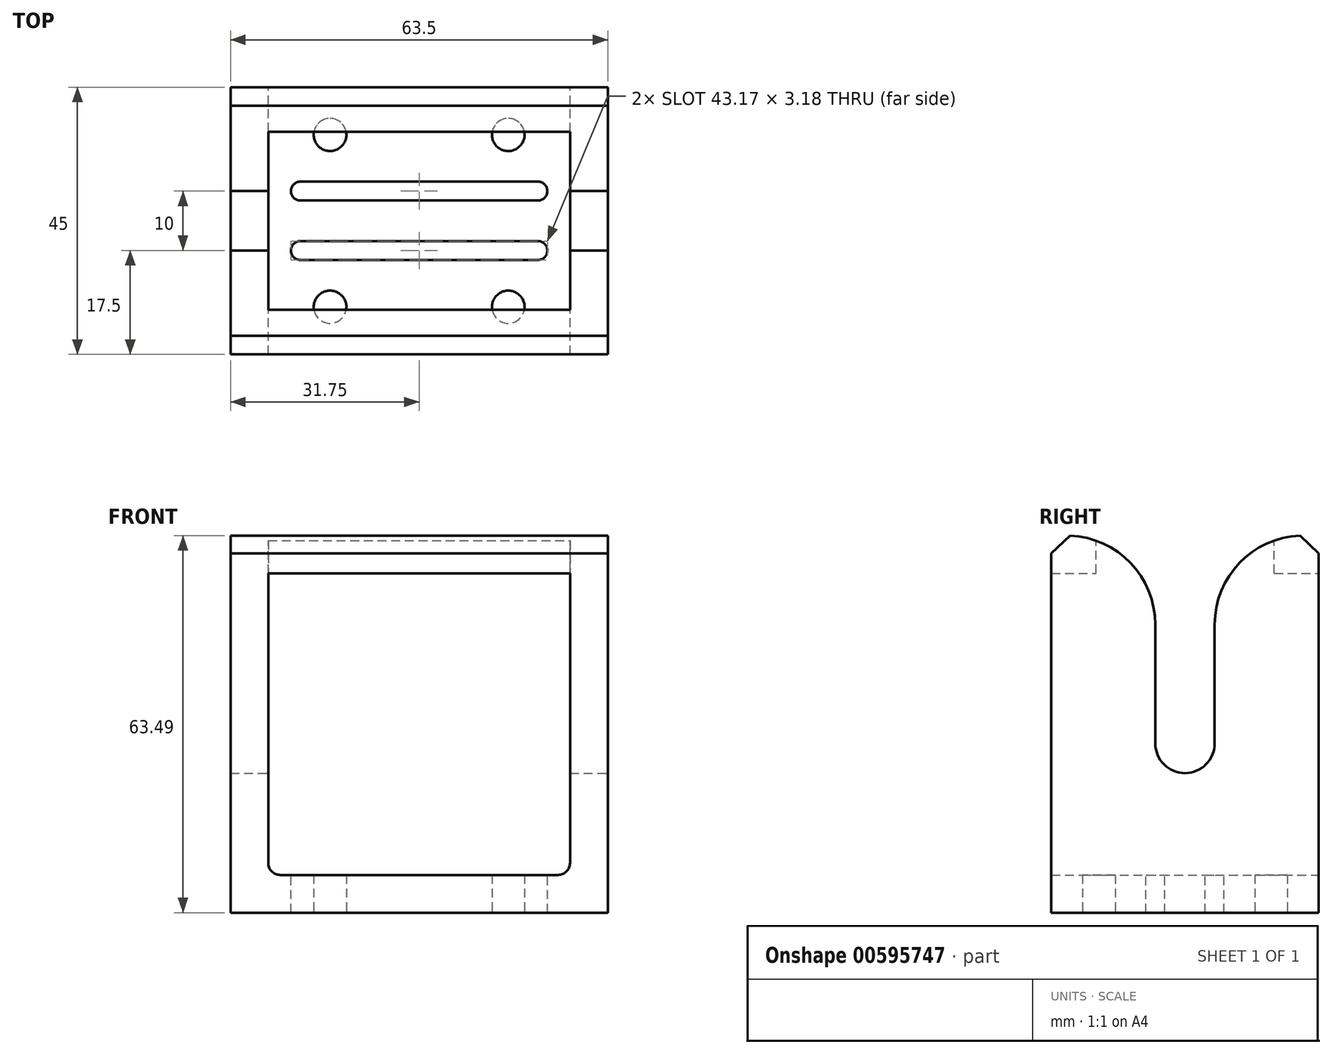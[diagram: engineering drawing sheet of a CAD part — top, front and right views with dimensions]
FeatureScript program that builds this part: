
annotation { "Feature Type Name" : "Feature", "Feature Type Description" : "" }
export const myFeature = defineFeature(function(context is Context, id is Id, definition is map)
    precondition{}
    {
        {
            var Q0;
            Q0=qCreatedBy(makeId("Front.planeOp"),FACE);
            var sketch = newSketch(context, id + "F0", { "sketchPlane" : qUnion([Q0])});
            skLineSegment(sketch, "E0", {"start": v(0, 0) * mm, "end": v(31.75, 0) * mm});
            skLineSegment(sketch, "E1", {"start": v(31.75, 0) * mm, "end": v(31.75, 63.5) * mm});
            skLineSegment(sketch, "E2", {"start": v(25.4, 57.15) * mm, "end": v(25.4, 6.35) * mm});
            skLineSegment(sketch, "E3", {"start": v(25.4, 6.35) * mm, "end": v(0, 6.35) * mm});
            skLineSegment(sketch, "E4", {"start": v(0, 6.35) * mm, "end": v(0, 0) * mm});
            skLineSegment(sketch, "E5", {"start": v(25.4, 57.15) * mm, "end": v(0, 57.15) * mm});
            skLineSegment(sketch, "E6", {"start": v(0, 57.15) * mm, "end": v(0, 63.5) * mm});
            skLineSegment(sketch, "E7", {"start": v(0, 63.5) * mm, "end": v(31.75, 63.5) * mm});
            skSolve(sketch);
        }
        {
            var Q0;
            Q0=makeQuery(id+"F0.imprint","IMPRINT",FACE,{"disambiguationData":[TD([[makeQuery(id+"F0.imprint","IMPRINT",EDGE,{"derivedFrom":sQuery(id+"F0.wireOp",EDGE,"E0")}),1.0]])]});
            extrude(context, id + "F1", {"entities" : qUnion([Q0]), "depth" : 45 * mm, "offsetDistance" : 25 * mm, "symmetric" : true});
        }
        {
            var Q0;
            Q0=makeQuery(id+"F1.opExtrude","SWEPT_FACE",FACE,{"disambiguationData":[OSD([sQuery(id+"F0.wireOp",EDGE,"E1")])]});
            var sketch = newSketch(context, id + "F2", { "sketchPlane" : qUnion([Q0])});
            skPoint(sketch, "E8", {"position": v(0, 0) * mm});
            skArc(sketch, "E9", {"start": v(5, 47.24) * mm, "mid": v(0, 52.24) * mm, "end": v(-5, 47.24) * mm, "construction": true});
            skLineSegment(sketch, "E10", {"start": v(-5, 47.24) * mm, "end": v(-5, 6.35) * mm, "construction": true});
            skLineSegment(sketch, "E11.0", {"start": v(-22.5, 6.35) * mm, "end": v(22.5, 6.35) * mm, "construction": true});
            skLineSegment(sketch, "E12", {"start": v(5, 47.24) * mm, "end": v(5, 6.35) * mm, "construction": true});
            skArc(sketch, "E13", {"start": v(5, 28.5) * mm, "mid": v(0, 23.5) * mm, "end": v(-5, 28.5) * mm});
            skLineSegment(sketch, "E14", {"start": v(-5, 28.5) * mm, "end": v(-5, 48.5) * mm});
            skLineSegment(sketch, "E15", {"start": v(5, 28.5) * mm, "end": v(5, 48.5) * mm});
            skArc(sketch, "E16", {"start": v(5, 48.5) * mm, "mid": v(9.4, 59.1) * mm, "end": v(20, 63.5) * mm});
            skArc(sketch, "E17", {"start": v(-5, 48.5) * mm, "mid": v(-9.4, 59.1) * mm, "end": v(-20, 63.5) * mm});
            skLineSegment(sketch, "E18", {"start": v(-20, 63.5) * mm, "end": v(20, 63.5) * mm});
            skSolve(sketch);
        }
        {
            var Q0;
            Q0=makeQuery(id+"F1.opExtrude","SWEPT_BODY",BODY,{"disambiguationData":[OSD([sQuery(id+"F0.wireOp",EDGE,"E0"),sQuery(id+"F0.wireOp",EDGE,"E1"),sQuery(id+"F0.wireOp",EDGE,"C00b1ODD-DF0h-D2k2-2Klx-7LYLyqmDbQ7s"),sQuery(id+"F0.wireOp",EDGE,"E2"),sQuery(id+"F0.wireOp",EDGE,"E3"),sQuery(id+"F0.wireOp",EDGE,"E4")])]});
            var Q1;
            Q1=qCreatedBy(makeId("Right.planeOp"),FACE);
            mirror(context, id + "F3", {"operationType" : NewBodyOperationType.ADD, "entities" : qUnion([Q0]), "mirrorPlane" : qUnion([Q1])});
        }
        {
            var Q0;
            Q0 = qSketchRegion(id + "F2", true);
            extrude(context, id + "F4", {"entities" : qUnion([Q0]), "operationType" : NewBodyOperationType.REMOVE, "endBound" : BoundingType.THROUGH_ALL, "oppositeDirection" : true, "depth" : 25 * mm, "offsetDistance" : 25 * mm});
        }
        {
            var Q0;
            Q0=makeQuery(id+"F3.opPattern","COPY",EDGE,{"derivedFrom":makeQuery(id+"F1.opExtrude","SWEPT_EDGE",EDGE,{"disambiguationData":[OSD([sQuery(id+"F0.wireOp",EDGE,"E2"),sQuery(id+"F0.wireOp",EDGE,"E3")])]}),"instanceName":"1"});
            var Q1;
            Q1=makeQuery(id+"F1.opExtrude","SWEPT_EDGE",EDGE,{"disambiguationData":[OSD([sQuery(id+"F0.wireOp",EDGE,"E2"),sQuery(id+"F0.wireOp",EDGE,"E3")])]});
            fillet(context, id + "F5", {"entities" : qUnion([Q0, Q1]), "radius" : 2 * mm, "tangentPropagation" : true, "allowEdgeOverflow" : false});
        }
        {
            var Q0;
            {var subQ0=makeQuery(id+"F1.opExtrude","SWEPT_FACE",FACE,{"disambiguationData":[OSD([sQuery(id+"F0.wireOp",EDGE,"E0")])]});Q0=makeQuery(id+"F3.boolean.opBoolean","MERGE",FACE,{"derivedFrom":[subQ0,makeQuery(id+"F3.opPattern","COPY",FACE,{"derivedFrom":subQ0,"instanceName":"1"})]});}
            var sketch = newSketch(context, id + "F6", { "sketchPlane" : qUnion([Q0])});
            skPoint(sketch, "E19", {"position": v(-15, -14.5) * mm});
            skPoint(sketch, "E20", {"position": v(15, 14.5) * mm});
            skLineSegment(sketch, "E21.bottom", {"start": v(15, -14.5) * mm, "end": v(-15, -14.5) * mm});
            skLineSegment(sketch, "E21.top", {"start": v(15, 14.5) * mm, "end": v(-15, 14.5) * mm});
            skLineSegment(sketch, "E21.left", {"start": v(15, -14.5) * mm, "end": v(15, 14.5) * mm});
            skLineSegment(sketch, "E21.right", {"start": v(-15, -14.5) * mm, "end": v(-15, 14.5) * mm});
            skPoint(sketch, "E21.middle", {"position": v(0, 0) * mm});
            skPoint(sketch, "E22", {"position": v(-15, 14.5) * mm});
            skPoint(sketch, "E23", {"position": v(15, -14.5) * mm});
            skSolve(sketch);
        }
        {
            var Q0;
            Q0=sQuery(id+"F6.wireOp",VERTEX,"E20");
            var Q1;
            Q1=sQuery(id+"F6.wireOp",VERTEX,"E19");
            var Q2;
            Q2=sQuery(id+"F6.wireOp",VERTEX,"E22");
            var Q3;
            Q3=sQuery(id+"F6.wireOp",VERTEX,"E23");
            var Q4;
            Q4=makeQuery(id+"F1.opExtrude","SWEPT_BODY",BODY,{"disambiguationData":[OSD([sQuery(id+"F0.wireOp",EDGE,"E0"),sQuery(id+"F0.wireOp",EDGE,"E1"),sQuery(id+"F0.wireOp",EDGE,"C00b1ODD-DF0h-D2k2-2Klx-7LYLyqmDbQ7s"),sQuery(id+"F0.wireOp",EDGE,"E2"),sQuery(id+"F0.wireOp",EDGE,"E3"),sQuery(id+"F0.wireOp",EDGE,"E4")])]});
            hole(context, id + "F7", {"style" : HoleStyle.SIMPLE, "endStyle" : HoleEndStyle.BLIND, "standardTappedOrClearance" : lookupTablePath({ "standard" : "ISO", "fit" : "Normal", "size" : "M5", "type" : "Clearance" }), "standardBlindInLast" : lookupTablePath({ "fit" : "Standard", "standard" : "ISO", "size" : "M5", "type" : "Clearance" }), "holeDiameter" : 5.5 * mm, "majorDiameter" : 6 * mm, "holeDepth" : 15 * mm, "isTappedThrough" : true, "tappedDepth" : 12 * mm, "tapClearance" : 3, "locations" : qUnion([Q0, Q1, Q2, Q3]), "scope" : qUnion([Q4])});
        }
        {
            var Q0;
            {var subQ0=makeQuery(id+"F1.opExtrude","SWEPT_FACE",FACE,{"disambiguationData":[OSD([sQuery(id+"F0.wireOp",EDGE,"E3")])]});Q0=makeQuery(id+"F3.boolean.opBoolean","MERGE",FACE,{"derivedFrom":[subQ0,makeQuery(id+"F3.opPattern","COPY",FACE,{"derivedFrom":subQ0,"instanceName":"1"})]});}
            var sketch = newSketch(context, id + "F8", { "sketchPlane" : qUnion([Q0])});
            skLineSegment(sketch, "E24.0", {"start": v(-31.75, -5) * mm, "end": v(-25.4, -5) * mm, "construction": true});
            skLineSegment(sketch, "E25", {"start": v(-20, -5) * mm, "end": v(20, -5) * mm, "construction": true});
            skPoint(sketch, "E26", {"position": v(0, -5) * mm});
            skArc(sketch, "E27", {"start": v(-20, -3.41) * mm, "mid": v(-21.59, -5) * mm, "end": v(-20, -6.59) * mm});
            skArc(sketch, "E28", {"start": v(20, -6.59) * mm, "mid": v(21.59, -5) * mm, "end": v(20, -3.41) * mm});
            skLineSegment(sketch, "E29", {"start": v(-20, -3.41) * mm, "end": v(20, -3.41) * mm});
            skLineSegment(sketch, "E30", {"start": v(20, -6.59) * mm, "end": v(-20, -6.59) * mm});
            skArc(sketch, "E31.MirrorCS", {"start": v(20, 6.59) * mm, "mid": v(21.59, 5) * mm, "end": v(20, 3.41) * mm});
            skLineSegment(sketch, "E32.MirrorCS", {"start": v(-20, 3.41) * mm, "end": v(20, 3.41) * mm});
            skLineSegment(sketch, "E33.MirrorCS", {"start": v(20, 6.59) * mm, "end": v(-20, 6.59) * mm});
            skArc(sketch, "E34.MirrorCS", {"start": v(-20, 3.41) * mm, "mid": v(-21.59, 5) * mm, "end": v(-20, 6.59) * mm});
            skSolve(sketch);
        }
        {
            var Q0;
            Q0 = qSketchRegion(id + "F8", true);
            extrude(context, id + "F9", {"entities" : qUnion([Q0]), "operationType" : NewBodyOperationType.REMOVE, "endBound" : BoundingType.THROUGH_ALL, "oppositeDirection" : true, "depth" : 25 * mm, "offsetDistance" : 25 * mm});
        }
        {
            var Q0;
            {var subQ2=sQuery(id+"F0.wireOp",EDGE,"E7");var subQ4=makeQuery(id+"F1.opExtrude","SWEPT_FACE",FACE,{"disambiguationData":[OSD([subQ2])]});Q0=makeQuery(id+"F4.boolean.opBoolean","SPLIT",FACE,{"disambiguationData":[TD([makeQuery(id+"F4.opExtrude","SWEPT_FACE",FACE,{"disambiguationData":[OSD([sQuery(id+"F2.wireOp",EDGE,"E17")])]})])],"derivedFrom":makeQuery(id+"F3.boolean.opBoolean","MERGE",FACE,{"derivedFrom":[subQ4,makeQuery(id+"F3.opPattern","COPY",FACE,{"derivedFrom":subQ4,"instanceName":"1"})]})});}
            var sketch = newSketch(context, id + "F10", { "sketchPlane" : qUnion([Q0])});
            skPoint(sketch, "E35.middle", {"position": v(0, 0) * mm});
            skLineSegment(sketch, "E36.0", {"start": v(-25.4, 5) * mm, "end": v(-25.4, -5) * mm, "construction": true});
            skLineSegment(sketch, "E37.0", {"start": v(25.4, -5) * mm, "end": v(25.4, 5) * mm, "construction": true});
            skLineSegment(sketch, "E38.bottom", {"start": v(-25.4, -15) * mm, "end": v(25.4, -15) * mm});
            skLineSegment(sketch, "E38.top", {"start": v(-25.4, 15) * mm, "end": v(25.4, 15) * mm});
            skLineSegment(sketch, "E38.left", {"start": v(-25.4, -15) * mm, "end": v(-25.4, 15) * mm});
            skLineSegment(sketch, "E38.right", {"start": v(25.4, -15) * mm, "end": v(25.4, 15) * mm});
            skSolve(sketch);
        }
        {
            var Q0;
            Q0 = qSketchRegion(id + "F10", true);
            var Q1;
            {var subQ0=sQuery(id+"F0.wireOp",EDGE,"E5");var subQ4=makeQuery(id+"F1.opExtrude","SWEPT_FACE",FACE,{"disambiguationData":[OSD([subQ0])]});Q1=makeQuery(id+"F4.boolean.opBoolean","SPLIT",FACE,{"disambiguationData":[TD([makeQuery(id+"F4.opExtrude","SWEPT_FACE",FACE,{"disambiguationData":[OSD([sQuery(id+"F2.wireOp",EDGE,"E17")])]})])],"derivedFrom":makeQuery(id+"F3.boolean.opBoolean","MERGE",FACE,{"derivedFrom":[subQ4,makeQuery(id+"F3.opPattern","COPY",FACE,{"derivedFrom":subQ4,"instanceName":"1"})]})});}
            extrude(context, id + "F11", {"entities" : qUnion([Q0]), "operationType" : NewBodyOperationType.REMOVE, "endBound" : BoundingType.UP_TO_SURFACE, "oppositeDirection" : true, "depth" : 25 * mm, "endBoundEntityFace" : qUnion([Q1]), "offsetDistance" : 25 * mm});
        }
        {
            var Q0;
            {var subQ0=makeQuery(id+"F1.opExtrude","CAP_EDGE",EDGE,{"disambiguationData":[OSD([sQuery(id+"F0.wireOp",EDGE,"E7")])],"isStart":false});Q0=makeQuery(id+"F3.boolean.opBoolean","MERGE",EDGE,{"derivedFrom":[subQ0,makeQuery(id+"F3.opPattern","COPY",EDGE,{"derivedFrom":subQ0,"instanceName":"1"})]});}
            var Q1;
            {var subQ0=makeQuery(id+"F1.opExtrude","CAP_EDGE",EDGE,{"disambiguationData":[OSD([sQuery(id+"F0.wireOp",EDGE,"E7")])],"isStart":true});Q1=makeQuery(id+"F3.boolean.opBoolean","MERGE",EDGE,{"derivedFrom":[subQ0,makeQuery(id+"F3.opPattern","COPY",EDGE,{"derivedFrom":subQ0,"instanceName":"1"})]});}
            chamfer(context, id + "F12", {"entities" : qUnion([Q0, Q1]), "width" : 3 * mm, "tangentPropagation" : true});
        }
    });
